# Revit family: KS, ALU-PU 80, DS 20, M 8-M10, Ø 15- 35
name_source: partatom
category: HLS-Bauteile
revit_build: Autodesk Revit 2017 (Build: 20190507_1515(x64)
units: mm (PartAtom-declared; Revit-internal decimal feet)

## family parameters
Arbeitsebenenbasiert = Ja
Beim Laden mit Abzugskörper schneiden = Nein
Bemaßung runder Anschluss = Durchmesser verwenden
Gemeinsam genutzt = Ja
Immer vertikal = Nein
Raumberechnungspunkt = Nein
Teiletyp = Normal

## types (5) — shared parameters
A = 39 mm  [stored 0.127953 ft]
Anschluss = M8/M10
Baustoffklasse = B2
DS = 20 mm  [stored 0.0656168 ft]
DVS = 17 mm
Dichte Kern = 80 kg/m³
Dichte Mantel = 2.700 kg/m³
Dicke Mantel = 0,08 mm
Dämmkörper = ALU/PU
Dämmstärke = 20 mm  [stored 0.0656168 ft]
Fabrikat = MEFA
Firma = MEFA Befestigungs- und Montagesysteme GmbH
HGA = 16 mm  [stored 0.0524934 ft]
Kurztext1 = Kälteschelle RG80 ALU/PU
L = 100 mm  [stored 0.328084 ft]
MB = 25 mm  [stored 0.082021 ft]
MD = 3 mm  [stored 0.00984252 ft]
Material = Stahl
Material Mantel = Alufolie
Materialname = S235
Mengeneinheit = St
Oberflaeche = galvanisch verzinkt
Rohrschellentyp = Maxima PSM
Schalenlänge = 100 mm
Vorgabe-Ansicht = 1219 mm
Wasserdampfdiffusionswiderstand = 18750 µ
Wärmeleitfähigkeit = 0.025 W/mK
max. Temperaturbeständigkeit = 120 °C
mittl. Nenndruckfestigkeit Kern = 0,5 N/mm²
stat. Belastung Kern = 0,1 N/mm²
vpe = 1 St

## per-type parameters (varying)
| type | AB | Anschlußhöhe | Artikelnummer | B | Breite | D | D0 | DF1 | DF2 | Dmax | Dmin | EAN | Gewicht | Gewicht pro Bauteil | H | Kurztext2 | R | RM | Rohraußendurchmesser Kupfer | Rohraußendurchmesser Stahl | S | max. zul. Last |
| Kälteschelle ALU-PU 80, DS 20, M8/M10, Ø 15 | 0 mm  [stored 0 ft] | 46 mm | 75601545 | 114 mm | 114 mm | 15 mm  [stored 0.0492126 ft] | 55 mm  [stored 0.180446 ft] | 25 mm  [stored 0.082021 ft] | 24 mm  [stored 0.0787402 ft] | 19 mm  [stored 0.062336 ft] | 15 mm  [stored 0.0492126 ft] | 4250928443328 | 0.26 kg | 0.26 kg | 77 mm  [stored 0.252625 ft] | 15 mm Iso 20 x 100 mm M8/M10 | 28 mm  [stored 0.0918635 ft] | 31 mm  [stored 0.101706 ft] |  | 15 mm | 89 mm  [stored 0.291995 ft] | 0.20 kN |
| Kälteschelle ALU-PU 80, DS 20, M8/M10, Ø 17,2- 18 | 3 mm  [stored 0.00984252 ft] | 45 mm | 7560172 | 114 mm | 114 mm | 18 mm  [stored 0.0590551 ft] | 58 mm  [stored 0.190289 ft] | 25 mm  [stored 0.082021 ft] | 24 mm  [stored 0.0787402 ft] | 19 mm  [stored 0.062336 ft] | 15 mm  [stored 0.0492126 ft] | 4250928443342 | 0.26 kg | 0.26 kg | 80 mm  [stored 0.262467 ft] | 17,2 mm Iso 20 x 100 mm M8/M10 | 29 mm  [stored 0.0951444 ft] | 32 mm  [stored 0.104987 ft] | 18 mm | 17,2 mm | 89 mm  [stored 0.291995 ft] | 0.20 kN |
| Kälteschelle ALU-PU 80, DS 20, M8/M10, Ø 21,3- 22 | 2 mm  [stored 0.00656168 ft] | 46 mm | 75602145 | 120 mm | 120 mm | 22 mm  [stored 0.0721785 ft] | 62 mm  [stored 0.203412 ft] | 25 mm  [stored 0.082021 ft] | 26 mm | 23 mm  [stored 0.0754593 ft] | 20 mm  [stored 0.0656168 ft] | 4250928443366 | 0.28 kg | 0.28 kg | 84 mm  [stored 0.275591 ft] | 21,3 mm Iso 20 x 100 mm M8/M10 | 31 mm  [stored 0.101706 ft] | 34 mm  [stored 0.111549 ft] | 22 mm | 21,3 mm | 95 mm  [stored 0.31168 ft] | 0.20 kN |
| Kälteschelle ALU-PU 80, DS 20, M8/M10, Ø 26,9- 28 | 2 mm  [stored 0.00656168 ft] | 46 mm | 7560275 | 129 mm | 129 mm | 28 mm  [stored 0.0918635 ft] | 68 mm | 26 mm | 27 mm  [stored 0.0885827 ft] | 30 mm  [stored 0.0984252 ft] | 26 mm | 4250928443397 | 0.29 kg | 0.29 kg | 90 mm | 26,9 mm Iso 20 x 100 mm M8/M10 | 34 mm  [stored 0.111549 ft] | 37 mm  [stored 0.121391 ft] | 28 mm | 26,9 mm | 103 mm | 0.30 kN |
| Kälteschelle ALU-PU 80, DS 20, M8/M10, Ø 33,7- 35 | 3 mm  [stored 0.00984252 ft] | 44 mm | 75603445 | 129 mm | 129 mm | 35 mm  [stored 0.114829 ft] | 75 mm | 24 mm  [stored 0.0787402 ft] | 23 mm  [stored 0.0754593 ft] | 36 mm  [stored 0.11811 ft] | 32 mm  [stored 0.104987 ft] | 4250928443403 | 0.29 kg | 0.29 kg | 97 mm | 33,7 mm Iso 20 x 100 mm M8/M10 | 38 mm  [stored 0.124672 ft] | 41 mm | 35 mm | 33,7 mm | 105 mm | 0.30 kN |

note: [stored X ft] marks values corroborated as IEEE doubles in the binary element streams (Revit-internal decimal feet)

## geometry (parser evidence)
native form markers: Sweep x4
no freeform markers — native parametric forms only
